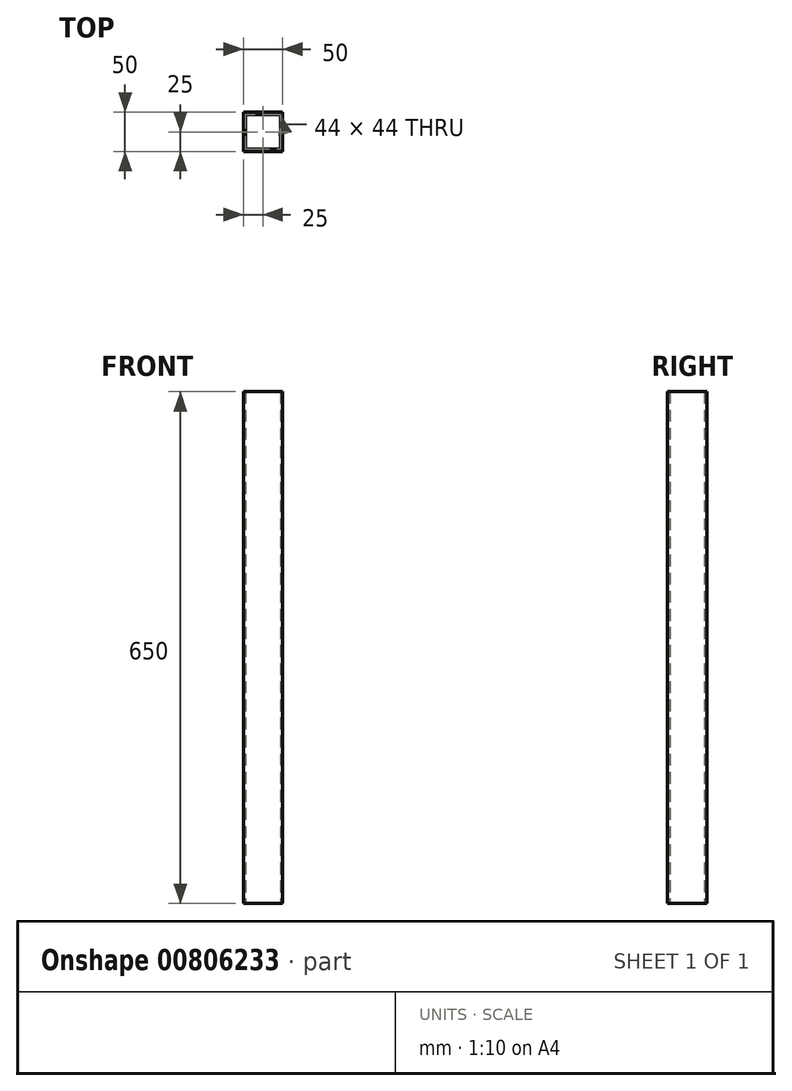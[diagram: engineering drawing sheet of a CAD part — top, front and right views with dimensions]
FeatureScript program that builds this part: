
annotation { "Feature Type Name" : "Feature", "Feature Type Description" : "" }
export const myFeature = defineFeature(function(context is Context, id is Id, definition is map)
    precondition{}
    {
        {
            var Q0;
            Q0=qCreatedBy(makeId("Top.planeOp"),FACE);
            var sketch = newSketch(context, id + "F0", { "sketchPlane" : qUnion([Q0])});
            skLineSegment(sketch, "E0.bottom", {"start": v(25, -25) * mm, "end": v(-25, -25) * mm});
            skLineSegment(sketch, "E0.top", {"start": v(25, 25) * mm, "end": v(-25, 25) * mm});
            skLineSegment(sketch, "E0.left", {"start": v(25, -25) * mm, "end": v(25, 25) * mm});
            skLineSegment(sketch, "E0.right", {"start": v(-25, -25) * mm, "end": v(-25, 25) * mm});
            skPoint(sketch, "E0.middle", {"position": v(0, 0) * mm});
            skLineSegment(sketch, "E1.0", {"start": v(-22, -22) * mm, "end": v(-22, 22) * mm});
            skLineSegment(sketch, "E1.1", {"start": v(22, -22) * mm, "end": v(-22, -22) * mm});
            skLineSegment(sketch, "E1.2", {"start": v(22, -22) * mm, "end": v(22, 22) * mm});
            skLineSegment(sketch, "E1.3", {"start": v(22, 22) * mm, "end": v(-22, 22) * mm});
            skSolve(sketch);
        }
        {
            var Q0;
            Q0=qSketchRegion(id+"F0",true);
            extrude(context, id + "F1", {"entities" : qUnion([Q0]), "depth" : 650 * mm, "offsetDistance" : 25 * mm});
        }
    });
